# Revit family: BE_70725_de_DE
name_source: partatom
category: Leuchten
units: mm (PartAtom-declared; Revit-internal decimal feet)

## family parameters
Basisbauteil = Fläche
Beim Laden mit Abzugskörper schneiden = Ja
Bemaßung runder Anschluss = Durchmesser verwenden
Gemeinsam genutzt = Nein
Lichtquelle = Nein
Raumberechnungspunkt = Ja
Teiletyp = Normal

## types (1)
- BEGA_70725_Grafit
    Aktualisierung = 2022-05-19T04:00:07
    BEGA_Dummy = Nein
    BEGA_IES = Ja
    BEGA_Intern = Ja
    BEGA_Intern_Konstruktion = Ja
    BEGA_Intern_an = Ja
    BEGA_Intern_aus = Ja
    Beschreibung = Lichtmast
    Beschreibung_Sonderanfertigung = Hier können Sie Informationen zur Sonderanfertigung eintragen.
    Bestellnummer = 70725
    CE_Konformität = ja
    Gewicht = 17.2 kg
    Hersteller = BEGA
    Lastklassifizierung = Beleuchtung
    Logo = BEGA_Logo.png
    M_A = Nein
    M_G = Ja
    M_W = Nein
    Material_02 = BEGA_Oberfläche_Silber_matt
    Material_03 = BEGA_Oberfläche_Weiss_matt
    Material_06 = BEGA_Oberfläche_Edelstahl_gebürstet
    Material_09 = BEGA_Glas_klar
    Material_11 = BEGA_Glas_opal
    Material_15 = BEGA_Leuchtmedium_matt
    Material_17 = BEGA_Reflektor
    Modell = 70725
    Produktdatenblatt = https://cdn.bega.com
    Scheinlast = 0 VA
    Sonderanfertigung = Nein
    Spannung = 0 V
    Typenbild = 70725.png
    URL = https://www.bega.com
    Vorgabe-Ansicht = 0 mm  [stored 0 ft]

note: [stored X ft] marks values corroborated as IEEE doubles in the binary element streams (Revit-internal decimal feet)
